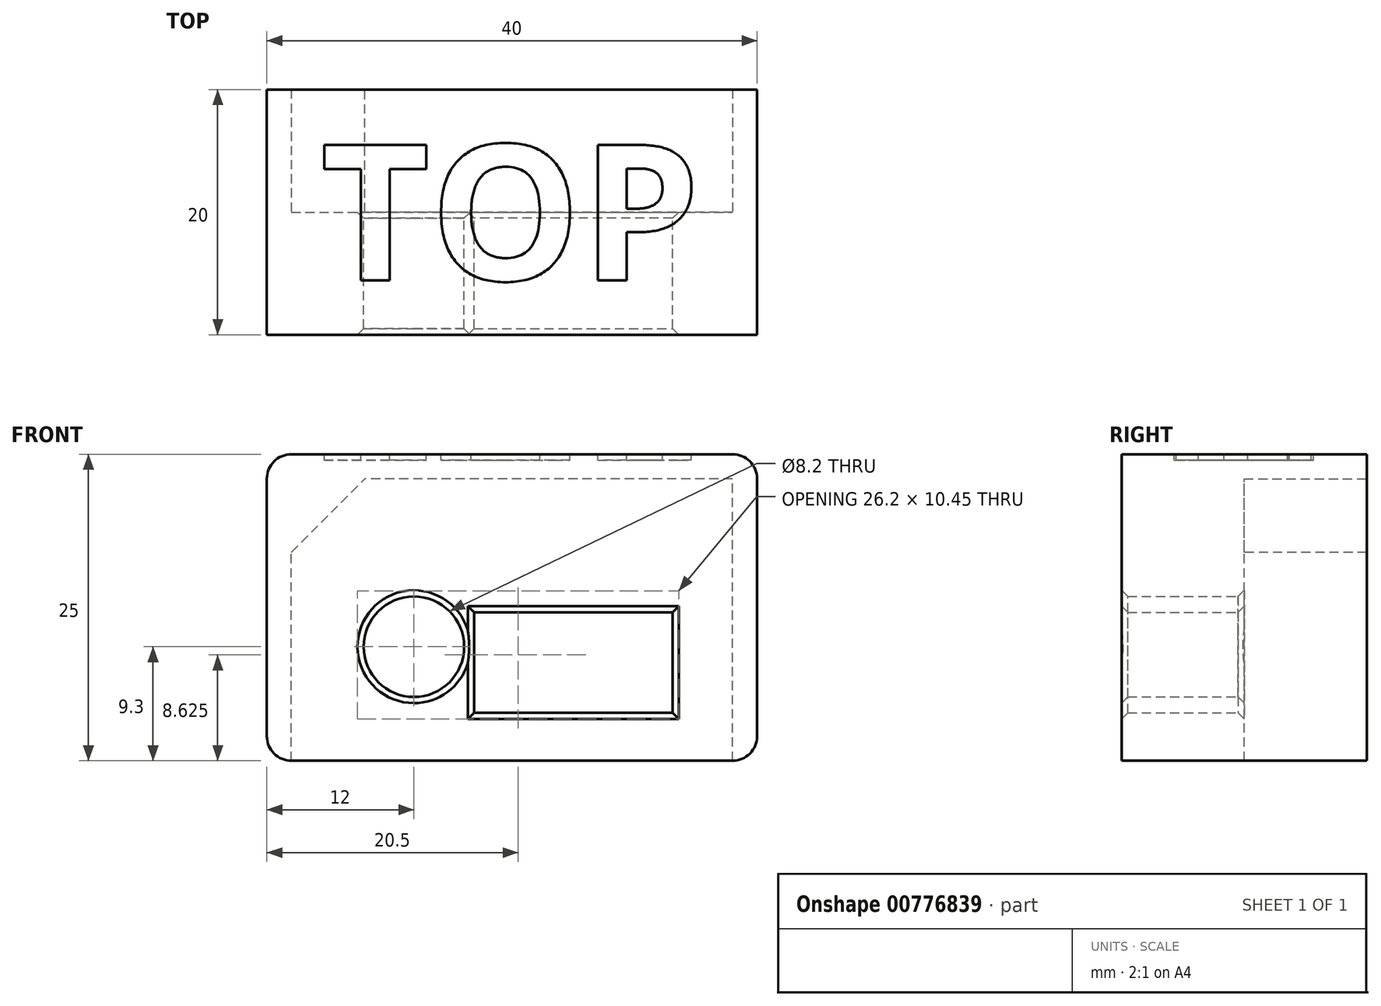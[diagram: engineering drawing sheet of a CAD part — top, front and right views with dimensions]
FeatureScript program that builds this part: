
annotation { "Feature Type Name" : "Feature", "Feature Type Description" : "" }
export const myFeature = defineFeature(function(context is Context, id is Id, definition is map)
    precondition{}
    {
        {
            var Q0;
            Q0=qCreatedBy(makeId("Front.planeOp"),FACE);
            var sketch = newSketch(context, id + "F0", { "sketchPlane" : qUnion([Q0])});
            skLineSegment(sketch, "E0.bottom", {"start": v(18, -11.5) * mm, "end": v(-18, -11.5) * mm});
            skLineSegment(sketch, "E0.top", {"start": v(18, 11.5) * mm, "end": v(-18, 11.5) * mm});
            skLineSegment(sketch, "E0.left", {"start": v(18, -11.5) * mm, "end": v(18, 11.5) * mm});
            skLineSegment(sketch, "E0.right", {"start": v(-18, -11.5) * mm, "end": v(-18, 11.5) * mm});
            skPoint(sketch, "E0.middle", {"position": v(0, 0) * mm});
            skPoint(sketch, "E1", {"position": v(5, -3.5) * mm});
            skLineSegment(sketch, "E2.bottom", {"start": v(13.1, -7.6) * mm, "end": v(-3.1, -7.6) * mm});
            skLineSegment(sketch, "E2.top", {"start": v(13.1, 0.6) * mm, "end": v(-3.1, 0.6) * mm});
            skLineSegment(sketch, "E2.left", {"start": v(13.1, -7.6) * mm, "end": v(13.1, 0.6) * mm});
            skLineSegment(sketch, "E2.right", {"start": v(-3.1, -7.6) * mm, "end": v(-3.1, 0.6) * mm});
            skPoint(sketch, "E3", {"position": v(-8, -2.2) * mm});
            skCircle(sketch, "E4", {"center": v(-8, -2.2) * mm, "radius": 4.1 * mm});
            skLineSegment(sketch, "E5", {"start": v(18, -11.5) * mm, "end": v(20, -11.5) * mm});
            skLineSegment(sketch, "E6", {"start": v(20, -11.5) * mm, "end": v(20, 13.5) * mm});
            skLineSegment(sketch, "E7", {"start": v(20, 13.5) * mm, "end": v(-20, 13.5) * mm});
            skLineSegment(sketch, "E8", {"start": v(-20, 13.5) * mm, "end": v(-20, -11.5) * mm});
            skLineSegment(sketch, "E9", {"start": v(-20, -11.5) * mm, "end": v(-18, -11.5) * mm});
            skSolve(sketch);
        }
        {
            var Q0;
            Q0 = qSketchRegion(id + "F0", true);
            extrude(context, id + "F1", {"entities" : qUnion([Q0]), "depth" : 10 * mm, "offsetDistance" : 25 * mm});
        }
        {
            var Q0;
            Q0=makeQuery(id+"F0.imprint","IMPRINT",FACE,{"disambiguationData":[TD([[makeQuery(id+"F0.imprint","IMPRINT",EDGE,{"derivedFrom":sQuery(id+"F0.wireOp",EDGE,"E0.top")}),-1.0]])]});
            extrude(context, id + "F2", {"entities" : qUnion([Q0]), "operationType" : NewBodyOperationType.ADD, "oppositeDirection" : true, "depth" : 10 * mm, "offsetDistance" : 25 * mm});
        }
        {
            var Q0;
            Q0=makeQuery(id+"F2.opExtrude","SWEPT_EDGE",EDGE,{"disambiguationData":[OSD([sQuery(id+"F0.wireOp",EDGE,"E0.top"),sQuery(id+"F0.wireOp",EDGE,"E0.right")])]});
            chamfer(context, id + "F3", {"entities" : qUnion([Q0]), "width" : 6 * mm, "tangentPropagation" : true});
        }
        {
            var Q0;
            {var subQ0=sQuery(id+"F0.wireOp",EDGE,"E8");var subQ1=sQuery(id+"F0.wireOp",EDGE,"E7");Q0=makeQuery(id+"F2.boolean.opBoolean","MERGE",EDGE,{"derivedFrom":[makeQuery(id+"F1.opExtrude","SWEPT_EDGE",EDGE,{"disambiguationData":[OSD([subQ1,subQ0])]}),makeQuery(id+"F2.opExtrude","SWEPT_EDGE",EDGE,{"disambiguationData":[OSD([subQ1,subQ0])]})]});}
            var Q1;
            {var subQ0=sQuery(id+"F0.wireOp",EDGE,"E7");var subQ1=sQuery(id+"F0.wireOp",EDGE,"E6");Q1=makeQuery(id+"F2.boolean.opBoolean","MERGE",EDGE,{"derivedFrom":[makeQuery(id+"F1.opExtrude","SWEPT_EDGE",EDGE,{"disambiguationData":[OSD([subQ1,subQ0])]}),makeQuery(id+"F2.opExtrude","SWEPT_EDGE",EDGE,{"disambiguationData":[OSD([subQ1,subQ0])]})]});}
            fillet(context, id + "F4", {"entities" : qUnion([Q0, Q1]), "radius" : 2 * mm, "tangentPropagation" : true, "allowEdgeOverflow" : false});
        }
        {
            var Q0;
            {var subQ0=sQuery(id+"F0.wireOp",EDGE,"E6");var subQ1=sQuery(id+"F0.wireOp",EDGE,"E5");Q0=makeQuery(id+"F2.boolean.opBoolean","MERGE",EDGE,{"derivedFrom":[makeQuery(id+"F1.opExtrude","SWEPT_EDGE",EDGE,{"disambiguationData":[OSD([subQ1,subQ0])]}),makeQuery(id+"F2.opExtrude","SWEPT_EDGE",EDGE,{"disambiguationData":[OSD([subQ1,subQ0])]})]});}
            var Q1;
            {var subQ0=sQuery(id+"F0.wireOp",EDGE,"E9");var subQ1=sQuery(id+"F0.wireOp",EDGE,"E8");Q1=makeQuery(id+"F2.boolean.opBoolean","MERGE",EDGE,{"derivedFrom":[makeQuery(id+"F1.opExtrude","SWEPT_EDGE",EDGE,{"disambiguationData":[OSD([subQ1,subQ0])]}),makeQuery(id+"F2.opExtrude","SWEPT_EDGE",EDGE,{"disambiguationData":[OSD([subQ1,subQ0])]})]});}
            fillet(context, id + "F5", {"entities" : qUnion([Q0, Q1]), "radius" : 2 * mm, "tangentPropagation" : true, "allowEdgeOverflow" : false});
        }
        {
            var Q0;
            {var subQ0=sQuery(id+"F0.wireOp",EDGE,"E7");Q0=makeQuery(id+"F2.boolean.opBoolean","MERGE",FACE,{"derivedFrom":[makeQuery(id+"F1.opExtrude","SWEPT_FACE",FACE,{"disambiguationData":[OSD([subQ0])]}),makeQuery(id+"F2.opExtrude","SWEPT_FACE",FACE,{"disambiguationData":[OSD([subQ0])]})]});}
            var sketch = newSketch(context, id + "F6", { "sketchPlane" : qUnion([Q0])});
            skText(sketch, "E10", { "text": "TOP", "fontName": "OpenSans-Bold.ttf"});
            const initialGuessF6  = {"E10": [-0.01563, -0.00556, 1, 0, 0.01113]};
            skSetInitialGuess(sketch, initialGuessF6);
            skSolve(sketch);
        }
        {
            var Q0;
            Q0 = qSketchRegion(id + "F6", true);
            extrude(context, id + "F7", {"entities" : qUnion([Q0]), "operationType" : NewBodyOperationType.REMOVE, "oppositeDirection" : true, "depth" : 0.5 * mm, "offsetDistance" : 25 * mm});
        }
        {
            var Q0;
            Q0=makeQuery(id+"F1.opExtrude","CAP_EDGE",EDGE,{"disambiguationData":[OSD([sQuery(id+"F0.wireOp",EDGE,"E2.left")])],"isStart":false});
            var Q1;
            Q1=makeQuery(id+"F1.opExtrude","CAP_EDGE",EDGE,{"disambiguationData":[OSD([sQuery(id+"F0.wireOp",EDGE,"E2.top")])],"isStart":false});
            var Q2;
            Q2=makeQuery(id+"F1.opExtrude","CAP_EDGE",EDGE,{"disambiguationData":[OSD([sQuery(id+"F0.wireOp",EDGE,"E2.right")])],"isStart":false});
            var Q3;
            Q3=makeQuery(id+"F1.opExtrude","CAP_EDGE",EDGE,{"disambiguationData":[OSD([sQuery(id+"F0.wireOp",EDGE,"E2.bottom")])],"isStart":false});
            var Q4;
            Q4=makeQuery(id+"F1.opExtrude","CAP_EDGE",EDGE,{"disambiguationData":[OSD([sQuery(id+"F0.wireOp",EDGE,"E4")])],"isStart":false});
            chamfer(context, id + "F8", {"entities" : qUnion([Q0, Q1, Q2, Q3, Q4]), "width" : 0.5 * mm, "tangentPropagation" : true});
        }
        {
            var Q0;
            Q0=makeQuery(id+"F1.opExtrude","CAP_EDGE",EDGE,{"disambiguationData":[OSD([sQuery(id+"F0.wireOp",EDGE,"E2.bottom")])],"isStart":true});
            var Q1;
            Q1=makeQuery(id+"F1.opExtrude","CAP_EDGE",EDGE,{"disambiguationData":[OSD([sQuery(id+"F0.wireOp",EDGE,"E2.right")])],"isStart":true});
            var Q2;
            Q2=makeQuery(id+"F1.opExtrude","CAP_EDGE",EDGE,{"disambiguationData":[OSD([sQuery(id+"F0.wireOp",EDGE,"E2.top")])],"isStart":true});
            var Q3;
            Q3=makeQuery(id+"F1.opExtrude","CAP_EDGE",EDGE,{"disambiguationData":[OSD([sQuery(id+"F0.wireOp",EDGE,"E2.left")])],"isStart":true});
            var Q4;
            Q4=makeQuery(id+"F1.opExtrude","CAP_EDGE",EDGE,{"disambiguationData":[OSD([sQuery(id+"F0.wireOp",EDGE,"E4")])],"isStart":true});
            chamfer(context, id + "F9", {"entities" : qUnion([Q0, Q1, Q2, Q3, Q4]), "width" : .5 * mm, "tangentPropagation" : true});
        }
    });
